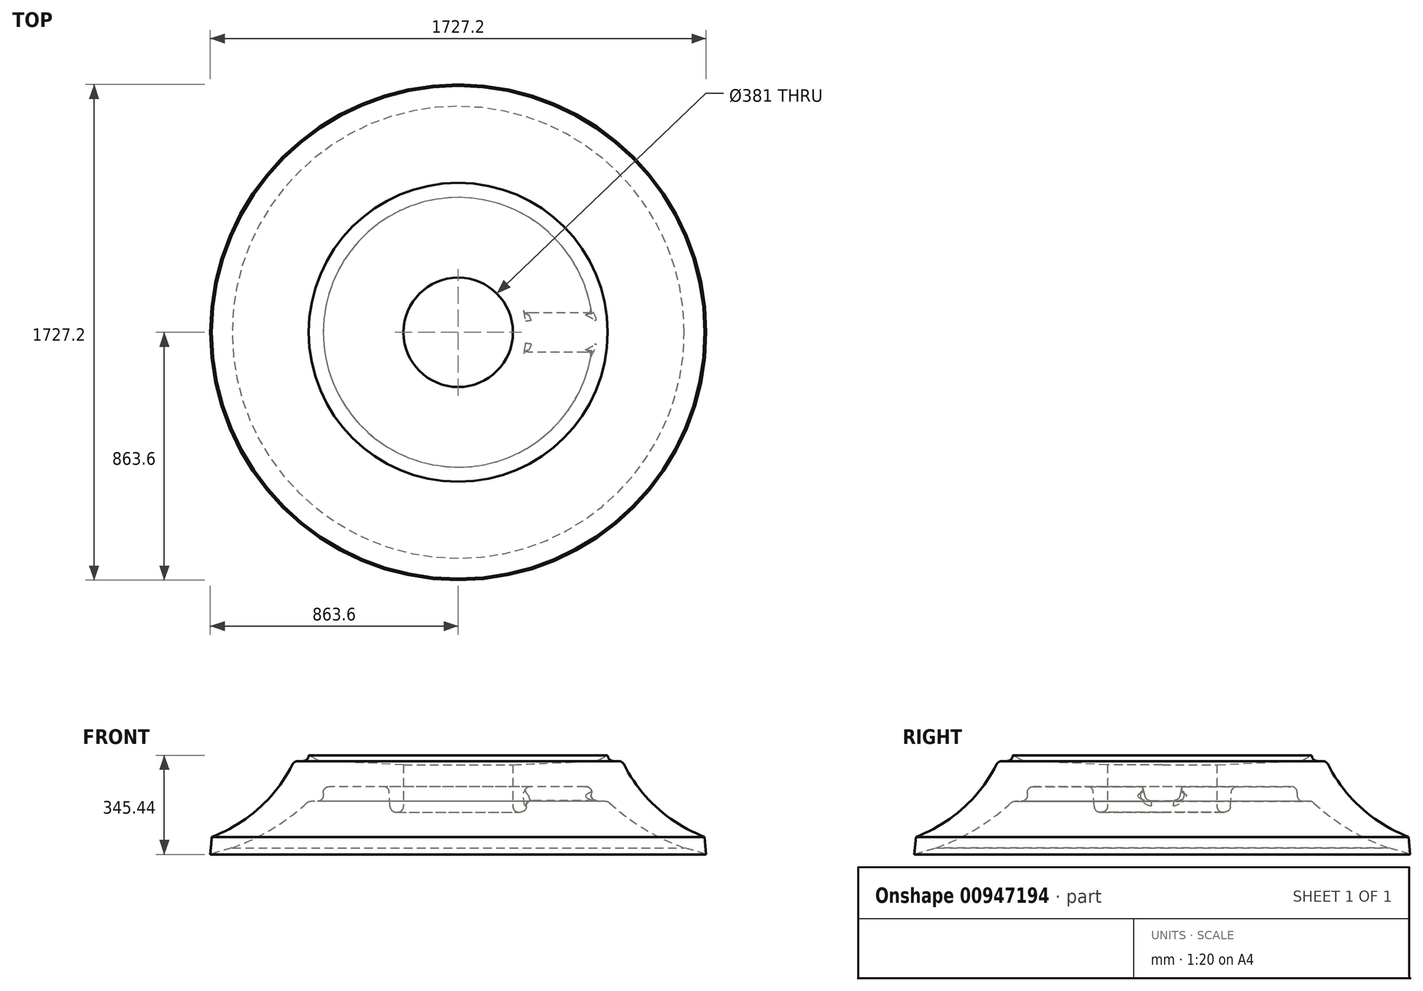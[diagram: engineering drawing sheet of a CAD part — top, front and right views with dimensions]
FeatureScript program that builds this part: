
annotation { "Feature Type Name" : "Feature", "Feature Type Description" : "" }
export const myFeature = defineFeature(function(context is Context, id is Id, definition is map)
    precondition{}
    {
        {
            var Q0;
            Q0=qCreatedBy(makeId("Front.planeOp"),FACE);
            var sketch = newSketch(context, id + "F0", { "sketchPlane" : qUnion([Q0])});
            skLineSegment(sketch, "E0", {"start": v(-190.5, 312.42) * mm, "end": v(-482.6, 325.12) * mm});
            skLineSegment(sketch, "E1", {"start": v(-482.6, 325.12) * mm, "end": v(-520.7, 345.44) * mm});
            skLineSegment(sketch, "E2", {"start": v(-520.7, 345.44) * mm, "end": v(-520.7, 325.12) * mm});
            skLineSegment(sketch, "E3", {"start": v(-520.7, 325.12) * mm, "end": v(-571.5, 325.12) * mm});
            skArc(sketch, "E4", {"start": v(-858.27, 60.96) * mm, "mid": v(-689.3, 165.27) * mm, "end": v(-571.5, 325.12) * mm});
            skLineSegment(sketch, "E5", {"start": v(-858.27, 60.96) * mm, "end": v(-863.6, 0) * mm});
            skLineSegment(sketch, "E6", {"start": v(-190.5, 312.42) * mm, "end": v(-190.5, 147.32) * mm});
            skLineSegment(sketch, "E7", {"start": v(0, 0) * mm, "end": v(0, 359.87) * mm, "construction": true});
            skLineSegment(sketch, "E8", {"start": v(-190.5, 147.32) * mm, "end": v(-236.22, 147.32) * mm});
            skArc(sketch, "E9", {"start": v(-787.4, 22.68) * mm, "mid": v(-645.62, 90.23) * mm, "end": v(-520.7, 185.42) * mm});
            skLineSegment(sketch, "E10", {"start": v(-520.7, 185.42) * mm, "end": v(-469.9, 185.42) * mm});
            skLineSegment(sketch, "E11", {"start": v(-469.9, 185.42) * mm, "end": v(-469.9, 236.22) * mm});
            skLineSegment(sketch, "E12", {"start": v(-469.9, 236.22) * mm, "end": v(-241.3, 236.22) * mm});
            skLineSegment(sketch, "E13", {"start": v(-236.22, 147.32) * mm, "end": v(-241.3, 236.22) * mm});
            skPoint(sketch, "E14.orphan", {"position": v(-190.5, 0) * mm});
            skArc(sketch, "E15", {"start": v(-787.4, 22.68) * mm, "mid": v(-825.72, 12.08) * mm, "end": v(-863.6, 0) * mm});
            skSolve(sketch);
        }
        {
            var Q0;
            Q0 = qSketchRegion(id + "F0", true);
            var Q1;
            Q1=sQuery(id+"F0.wireOp",EDGE,"E7");
            revolve(context, id + "F1", {"surfaceOperationType" : NewSurfaceOperationType.NEW, "entities" : qUnion([Q0]), "axis" : qUnion([Q1]), "revolveType" : RevolveType.FULL});
        }
        {
            var Q0;
            Q0=qCreatedBy(makeId("Right.planeOp"),FACE);
            cPlane(context, id + "F2", {"entities" : qUnion([Q0]), "cplaneType" : CPlaneType.OFFSET, "offset" : 198.12 * mm, "width" : 152.4 * mm, "height" : 152.4 * mm});
        }
        {
            var Q0;
            Q0=qCreatedBy(id+"F2.planeOp",FACE);
            var sketch = newSketch(context, id + "F3", { "sketchPlane" : qUnion([Q0])});
            skLineSegment(sketch, "E16", {"start": v(-69.85, 238.76) * mm, "end": v(-57.15, 187.96) * mm});
            skLineSegment(sketch, "E17", {"start": v(-57.15, 187.96) * mm, "end": v(57.15, 187.96) * mm});
            skLineSegment(sketch, "E18", {"start": v(57.15, 187.96) * mm, "end": v(69.85, 238.76) * mm});
            skLineSegment(sketch, "E19", {"start": v(69.85, 238.76) * mm, "end": v(-69.85, 238.76) * mm});
            skSolve(sketch);
        }
        {
            var Q0;
            Q0=makeQuery(id+"F1.opRevolve","SWEPT_EDGE",EDGE,{"disambiguationData":[OSD([sQuery(id+"F0.wireOp",EDGE,"E11"),sQuery(id+"F0.wireOp",EDGE,"E12")])]});
            var Q1;
            Q1=makeQuery(id+"F1.opRevolve","SWEPT_EDGE",EDGE,{"disambiguationData":[OSD([sQuery(id+"F0.wireOp",EDGE,"E10"),sQuery(id+"F0.wireOp",EDGE,"E11")])]});
            var Q2;
            Q2=makeQuery(id+"F1.opRevolve","SWEPT_EDGE",EDGE,{"disambiguationData":[OSD([sQuery(id+"F0.wireOp",EDGE,"E9"),sQuery(id+"F0.wireOp",EDGE,"E10")])]});
            var Q3;
            Q3=makeQuery(id+"F1.opRevolve","SWEPT_FACE",FACE,{"disambiguationData":[OSD([sQuery(id+"F0.wireOp",EDGE,"E3")])]});
            var Q4;
            Q4=makeQuery(id+"F1.opRevolve","SWEPT_EDGE",EDGE,{"disambiguationData":[OSD([sQuery(id+"F0.wireOp",EDGE,"E0"),sQuery(id+"F0.wireOp",EDGE,"E1")])]});
            var Q5;
            Q5=makeQuery(id+"F1.opRevolve","SWEPT_EDGE",EDGE,{"disambiguationData":[OSD([sQuery(id+"F0.wireOp",EDGE,"E8"),sQuery(id+"F0.wireOp",EDGE,"E13")])]});
            var Q6;
            Q6=makeQuery(id+"F1.opRevolve","SWEPT_EDGE",EDGE,{"disambiguationData":[OSD([sQuery(id+"F0.wireOp",EDGE,"E6"),sQuery(id+"F0.wireOp",EDGE,"E8")])]});
            var Q7;
            Q7=makeQuery(id+"F1.opRevolve","SWEPT_EDGE",EDGE,{"disambiguationData":[OSD([sQuery(id+"F0.wireOp",EDGE,"E12"),sQuery(id+"F0.wireOp",EDGE,"E13")])]});
            fillet(context, id + "F4", {"entities" : qUnion([Q0, Q1, Q2, Q3, Q4, Q5, Q6, Q7]), "radius" : 20.32 * mm, "tangentPropagation" : true, "allowEdgeOverflow" : false});
        }
        {
            var Q0;
            Q0 = qSketchRegion(id + "F3", true);
            extrude(context, id + "F5", {"entities" : qUnion([Q0]), "operationType" : NewBodyOperationType.ADD, "depth" : 304.8 * mm, "offsetDistance" : 25.4 * mm});
        }
        {
            var Q0;
            Q0=makeQuery(id+"FuPMPjmN6IqmVU1_1.-5.F5.opExtrude","SWEPT_FACE",FACE,{"disambiguationData":[OSD([sQuery(id+"F3.wireOp",EDGE,"E17")])]});
            var Q1;
            Q1=makeQuery(id+"FuPMPjmN6IqmVU1_1.-6.F5.opExtrude","SWEPT_FACE",FACE,{"disambiguationData":[OSD([sQuery(id+"F3.wireOp",EDGE,"E17")])]});
            var Q2;
            Q2=makeQuery(id+"FuPMPjmN6IqmVU1_1.-7.F5.opExtrude","SWEPT_FACE",FACE,{"disambiguationData":[OSD([sQuery(id+"F3.wireOp",EDGE,"E17")])]});
            var Q3;
            Q3=makeQuery(id+"F5.opExtrude","SWEPT_FACE",FACE,{"disambiguationData":[OSD([sQuery(id+"F3.wireOp",EDGE,"E17")])]});
            var Q4;
            Q4=makeQuery(id+"FuPMPjmN6IqmVU1_1.-1.F5.opExtrude","SWEPT_FACE",FACE,{"disambiguationData":[OSD([sQuery(id+"F3.wireOp",EDGE,"E17")])]});
            var Q5;
            Q5=makeQuery(id+"FuPMPjmN6IqmVU1_1.-2.F5.opExtrude","SWEPT_FACE",FACE,{"disambiguationData":[OSD([sQuery(id+"F3.wireOp",EDGE,"E17")])]});
            var Q6;
            Q6=makeQuery(id+"FuPMPjmN6IqmVU1_1.-3.F5.opExtrude","SWEPT_FACE",FACE,{"disambiguationData":[OSD([sQuery(id+"F3.wireOp",EDGE,"E17")])]});
            var Q7;
            Q7=makeQuery(id+"FuPMPjmN6IqmVU1_1.-4.F5.opExtrude","SWEPT_FACE",FACE,{"disambiguationData":[OSD([sQuery(id+"F3.wireOp",EDGE,"E17")])]});
            fillet(context, id + "F6", {"entities" : qUnion([Q0, Q1, Q2, Q3, Q4, Q5, Q6, Q7]), "radius" : 20.32 * mm, "tangentPropagation" : true, "allowEdgeOverflow" : false});
        }
    });
